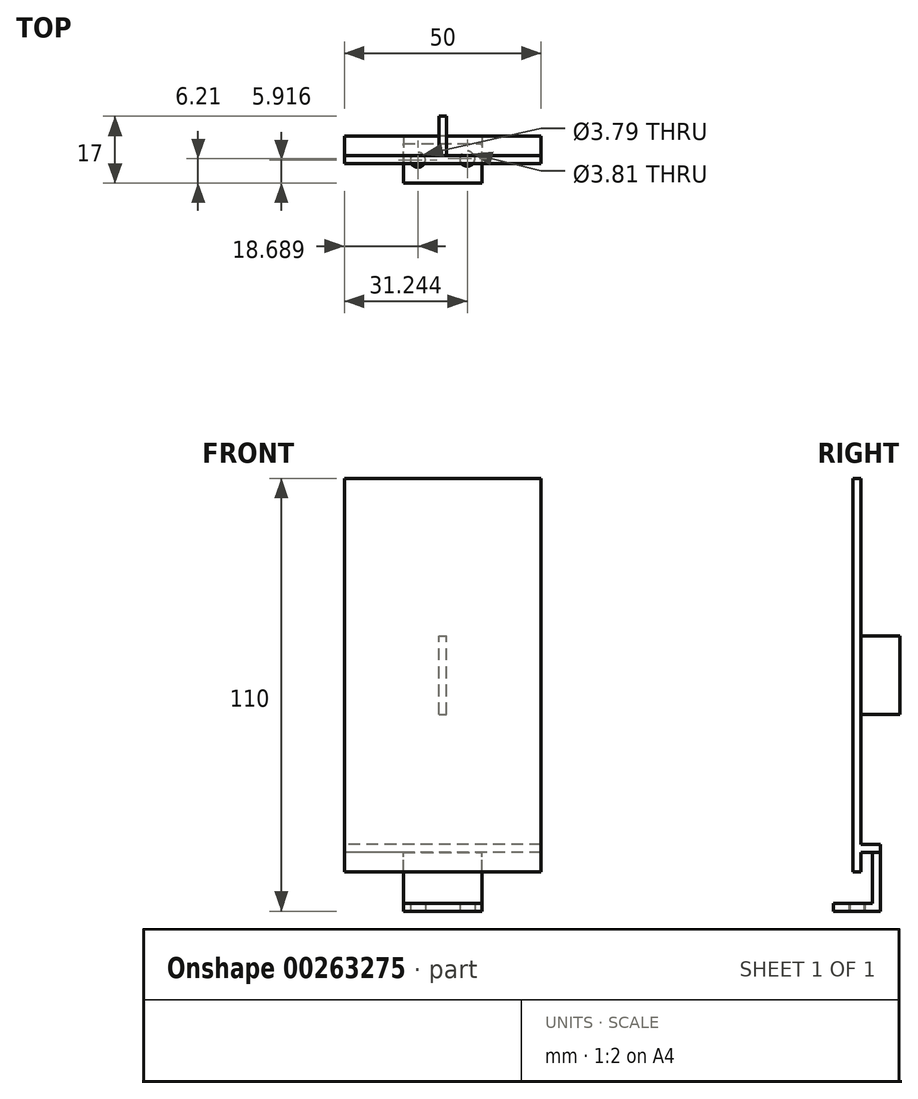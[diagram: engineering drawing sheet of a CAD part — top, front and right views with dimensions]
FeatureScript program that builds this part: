
annotation { "Feature Type Name" : "Feature", "Feature Type Description" : "" }
export const myFeature = defineFeature(function(context is Context, id is Id, definition is map)
    precondition{}
    {
        {
            var Q0;
            Q0=qCreatedBy(makeId("Front.planeOp"),FACE);
            var sketch = newSketch(context, id + "F0", { "sketchPlane" : qUnion([Q0])});
            skLineSegment(sketch, "E0.bottom", {"start": v(25, -50) * mm, "end": v(-25, -50) * mm});
            skLineSegment(sketch, "E0.top", {"start": v(25, 50) * mm, "end": v(-25, 50) * mm});
            skLineSegment(sketch, "E0.left", {"start": v(25, -50) * mm, "end": v(25, 50) * mm});
            skLineSegment(sketch, "E0.right", {"start": v(-25, -50) * mm, "end": v(-25, 50) * mm});
            skPoint(sketch, "E0.middle", {"position": v(0, 0) * mm});
            skSolve(sketch);
        }
        {
            var Q0;
            Q0 = qSketchRegion(id + "F0", true);
            extrude(context, id + "F1", {"entities" : qUnion([Q0]), "depth" : 2 * mm});
        }
        {
            var Q0;
            Q0=makeQuery(id+"F1.opExtrude","CAP_FACE",FACE,{"disambiguationData":[OSD([sQuery(id+"F0.wireOp",EDGE,"E0.bottom"),sQuery(id+"F0.wireOp",EDGE,"E0.top"),sQuery(id+"F0.wireOp",EDGE,"E0.left"),sQuery(id+"F0.wireOp",EDGE,"E0.right")])],"isStart":true});
            var sketch = newSketch(context, id + "F2", { "sketchPlane" : qUnion([Q0])});
            skLineSegment(sketch, "E1.bottom", {"start": v(-25, -45) * mm, "end": v(25, -45) * mm});
            skLineSegment(sketch, "E1.top", {"start": v(-25, -43) * mm, "end": v(25, -43) * mm});
            skLineSegment(sketch, "E1.left", {"start": v(-25, -45) * mm, "end": v(-25, -43) * mm});
            skLineSegment(sketch, "E1.right", {"start": v(25, -45) * mm, "end": v(25, -43) * mm});
            skSolve(sketch);
        }
        {
            var Q0;
            Q0 = qSketchRegion(id + "F2", true);
            extrude(context, id + "F3", {"entities" : qUnion([Q0]), "operationType" : NewBodyOperationType.ADD, "depth" : 5 * mm});
        }
        {
            var Q0;
            Q0=makeQuery(id+"F3.opExtrude","SWEPT_FACE",FACE,{"disambiguationData":[OSD([sQuery(id+"F2.wireOp",EDGE,"E1.bottom")])]});
            var sketch = newSketch(context, id + "F4", { "sketchPlane" : qUnion([Q0])});
            skLineSegment(sketch, "E2.bottom", {"start": v(0, -5) * mm, "end": v(10, -5) * mm});
            skLineSegment(sketch, "E2.top", {"start": v(0, -3) * mm, "end": v(10, -3) * mm});
            skLineSegment(sketch, "E2.left", {"start": v(0, -5) * mm, "end": v(0, -3) * mm});
            skLineSegment(sketch, "E2.right", {"start": v(10, -5) * mm, "end": v(10, -3) * mm});
            skSolve(sketch);
        }
        {
            var Q0;
            Q0 = qSketchRegion(id + "F4", true);
            extrude(context, id + "F5", {"entities" : qUnion([Q0]), "operationType" : NewBodyOperationType.ADD, "depth" : 15 * mm});
        }
        {
            var Q0;
            Q0=makeQuery(id+"F3.opExtrude","SWEPT_FACE",FACE,{"disambiguationData":[OSD([sQuery(id+"F2.wireOp",EDGE,"E1.bottom")])]});
            var sketch = newSketch(context, id + "F6", { "sketchPlane" : qUnion([Q0])});
            skLineSegment(sketch, "E3.bottom", {"start": v(0, -5) * mm, "end": v(-10, -5) * mm});
            skLineSegment(sketch, "E3.top", {"start": v(0, -3) * mm, "end": v(-10, -3) * mm});
            skLineSegment(sketch, "E3.left", {"start": v(0, -5) * mm, "end": v(0, -3) * mm});
            skLineSegment(sketch, "E3.right", {"start": v(-10, -5) * mm, "end": v(-10, -3) * mm});
            skSolve(sketch);
        }
        {
            var Q0;
            Q0 = qSketchRegion(id + "F6", true);
            extrude(context, id + "F7", {"entities" : qUnion([Q0]), "operationType" : NewBodyOperationType.ADD, "depth" : 15 * mm});
        }
        {
            var Q0;
            Q0=makeQuery(id+"F7.boolean.opBoolean","MERGE",FACE,{"derivedFrom":[makeQuery(id+"F5.opExtrude","SWEPT_FACE",FACE,{"disambiguationData":[OSD([sQuery(id+"F4.wireOp",EDGE,"E2.top")])]}),makeQuery(id+"F7.opExtrude","SWEPT_FACE",FACE,{"disambiguationData":[OSD([sQuery(id+"F6.wireOp",EDGE,"E3.top")])]})]});
            var sketch = newSketch(context, id + "F8", { "sketchPlane" : qUnion([Q0])});
            skLineSegment(sketch, "E4.bottom", {"start": v(-10, -60) * mm, "end": v(10, -60) * mm});
            skLineSegment(sketch, "E4.top", {"start": v(-10, -58) * mm, "end": v(10, -58) * mm});
            skLineSegment(sketch, "E4.left", {"start": v(-10, -60) * mm, "end": v(-10, -58) * mm});
            skLineSegment(sketch, "E4.right", {"start": v(10, -60) * mm, "end": v(10, -58) * mm});
            skSolve(sketch);
        }
        {
            var Q0;
            Q0 = qSketchRegion(id + "F8", true);
            extrude(context, id + "F9", {"entities" : qUnion([Q0]), "operationType" : NewBodyOperationType.ADD, "depth" : 10 * mm});
        }
        {
            var Q0;
            Q0=makeQuery(id+"F9.boolean.opBoolean","MERGE",FACE,{"derivedFrom":[makeQuery(id+"F7.boolean.opBoolean","MERGE",FACE,{"derivedFrom":[makeQuery(id+"F5.opExtrude","CAP_FACE",FACE,{"disambiguationData":[OSD([sQuery(id+"F4.wireOp",EDGE,"E2.bottom"),sQuery(id+"F4.wireOp",EDGE,"E2.top"),sQuery(id+"F4.wireOp",EDGE,"E2.left"),sQuery(id+"F4.wireOp",EDGE,"E2.right")])],"isStart":false}),makeQuery(id+"F7.opExtrude","CAP_FACE",FACE,{"disambiguationData":[OSD([sQuery(id+"F6.wireOp",EDGE,"E3.bottom"),sQuery(id+"F6.wireOp",EDGE,"E3.top"),sQuery(id+"F6.wireOp",EDGE,"E3.left"),sQuery(id+"F6.wireOp",EDGE,"E3.right")])],"isStart":false})]}),makeQuery(id+"F9.opExtrude","SWEPT_FACE",FACE,{"disambiguationData":[OSD([sQuery(id+"F8.wireOp",EDGE,"E4.bottom")])]})]});
            var sketch = newSketch(context, id + "F10", { "sketchPlane" : qUnion([Q0])});
            skCircle(sketch, "E5", {"center": v(-6.31, 1.08) * mm, "radius": 1.9 * mm});
            skSolve(sketch);
        }
        {
            var Q0;
            Q0 = qSketchRegion(id + "F10", true);
            extrude(context, id + "F11", {"entities" : qUnion([Q0]), "operationType" : NewBodyOperationType.REMOVE, "oppositeDirection" : true, "depth" : 3 * mm});
        }
        {
            var Q0;
            Q0=makeQuery(id+"F9.boolean.opBoolean","MERGE",FACE,{"derivedFrom":[makeQuery(id+"F7.boolean.opBoolean","MERGE",FACE,{"derivedFrom":[makeQuery(id+"F5.opExtrude","CAP_FACE",FACE,{"disambiguationData":[OSD([sQuery(id+"F4.wireOp",EDGE,"E2.bottom"),sQuery(id+"F4.wireOp",EDGE,"E2.top"),sQuery(id+"F4.wireOp",EDGE,"E2.left"),sQuery(id+"F4.wireOp",EDGE,"E2.right")])],"isStart":false}),makeQuery(id+"F7.opExtrude","CAP_FACE",FACE,{"disambiguationData":[OSD([sQuery(id+"F6.wireOp",EDGE,"E3.bottom"),sQuery(id+"F6.wireOp",EDGE,"E3.top"),sQuery(id+"F6.wireOp",EDGE,"E3.left"),sQuery(id+"F6.wireOp",EDGE,"E3.right")])],"isStart":false})]}),makeQuery(id+"F9.opExtrude","SWEPT_FACE",FACE,{"disambiguationData":[OSD([sQuery(id+"F8.wireOp",EDGE,"E4.bottom")])]})]});
            var sketch = newSketch(context, id + "F12", { "sketchPlane" : qUnion([Q0])});
            skCircle(sketch, "E6", {"center": v(6.24, 0.8) * mm, "radius": 1.9 * mm});
            skSolve(sketch);
        }
        {
            var Q0;
            Q0 = qSketchRegion(id + "F12", true);
            extrude(context, id + "F13", {"entities" : qUnion([Q0]), "operationType" : NewBodyOperationType.REMOVE, "oppositeDirection" : true, "depth" : 3 * mm});
        }
        {
            var Q0;
            {var subQ0=sQuery(id+"F0.wireOp",EDGE,"E0.left");var subQ1=sQuery(id+"F0.wireOp",EDGE,"E0.right");var subQ2=sQuery(id+"F0.wireOp",EDGE,"E0.top");Q0=makeQuery(id+"F3.boolean.opBoolean","SPLIT",FACE,{"disambiguationData":[TD([makeQuery(id+"F1.opExtrude","SWEPT_FACE",FACE,{"disambiguationData":[OSD([subQ2])]})])],"derivedFrom":makeQuery(id+"F1.opExtrude","CAP_FACE",FACE,{"disambiguationData":[OSD([sQuery(id+"F0.wireOp",EDGE,"E0.bottom"),subQ2,subQ0,subQ1])],"isStart":true})});}
            var sketch = newSketch(context, id + "F14", { "sketchPlane" : qUnion([Q0])});
            skLineSegment(sketch, "E7.bottom", {"start": v(1, -10) * mm, "end": v(-1, -10) * mm});
            skLineSegment(sketch, "E7.top", {"start": v(1, 10) * mm, "end": v(-1, 10) * mm});
            skLineSegment(sketch, "E7.left", {"start": v(1, -10) * mm, "end": v(1, 10) * mm});
            skLineSegment(sketch, "E7.right", {"start": v(-1, -10) * mm, "end": v(-1, 10) * mm});
            skPoint(sketch, "E7.middle", {"position": v(0, 0) * mm});
            skSolve(sketch);
        }
        {
            var Q0;
            Q0 = qSketchRegion(id + "F14", true);
            extrude(context, id + "F15", {"entities" : qUnion([Q0]), "operationType" : NewBodyOperationType.ADD, "depth" : 10 * mm});
        }
    });
